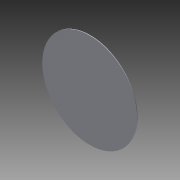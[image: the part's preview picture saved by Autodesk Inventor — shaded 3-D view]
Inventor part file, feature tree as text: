
AUTODESK INVENTOR PART (.ipt)
format: ipt  version: 2015 (Build 190159000, 159)  size: 71,168 bytes
history: native  units: mm
features: extrude x1, sketch x1
ambient origin geometry x8: Origin, YZ Plane, XZ Plane, XY Plane, X Axis, Y Axis, Z Axis, Center Point
bodies: Solid1 (feature_tree)
feature tree (2):
  extrude  "Extrusion1"  Depth=4.0mm TaperAngle=0.0deg
  sketch  "Sketch1"  dims[d0=600.0mm d1=4.0mm d2=0.0mm]
